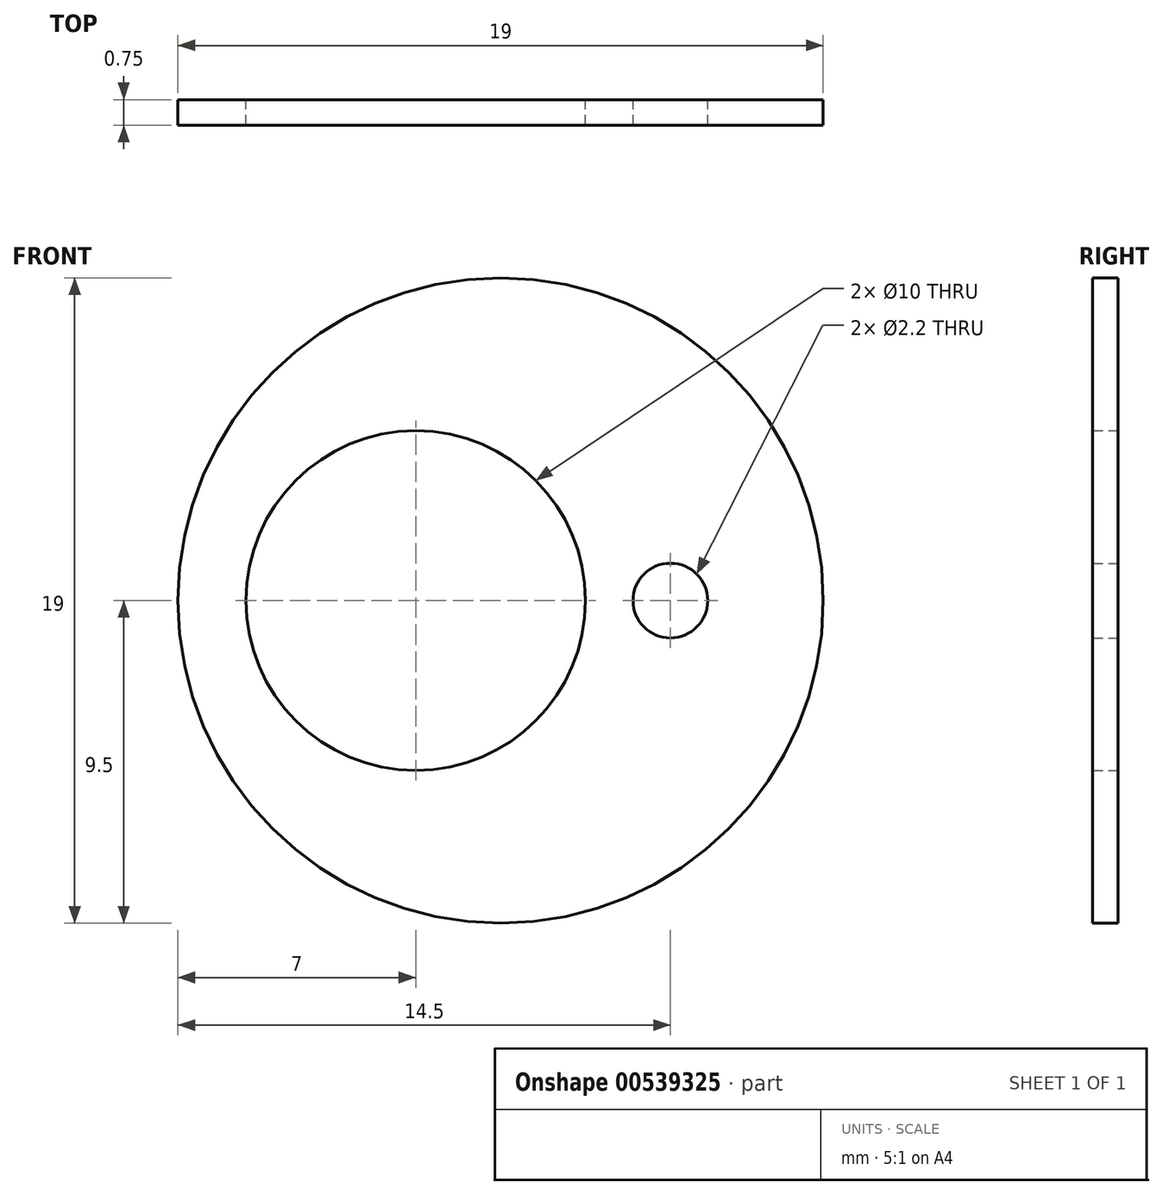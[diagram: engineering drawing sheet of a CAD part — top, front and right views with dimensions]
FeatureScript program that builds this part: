
annotation { "Feature Type Name" : "Feature", "Feature Type Description" : "" }
export const myFeature = defineFeature(function(context is Context, id is Id, definition is map)
    precondition{}
    {
        {
            var Q0;
            Q0=qCreatedBy(makeId("Front.planeOp"),FACE);
            var sketch = newSketch(context, id + "F0", { "sketchPlane" : qUnion([Q0])});
            skCircle(sketch, "E0", {"center": v(0, 0) * mm, "radius": 9.5 * mm});
            skLineSegment(sketch, "E1", {"start": v(0, 9.5) * mm, "end": v(0, -9.5) * mm, "construction": true});
            skLineSegment(sketch, "E2", {"start": v(-9.5, 0) * mm, "end": v(9.5, 0) * mm, "construction": true});
            skPoint(sketch, "E3", {"position": v(5, 0) * mm});
            skPoint(sketch, "E4", {"position": v(-2.5, 0) * mm});
            skCircle(sketch, "E5", {"center": v(-2.5, 0) * mm, "radius": 5 * mm});
            skCircle(sketch, "E6", {"center": v(5, 0) * mm, "radius": 1.1 * mm});
            skSolve(sketch);
        }
        {
            var Q0;
            Q0 = qSketchRegion(id + "F0", true);
            extrude(context, id + "F1", {"entities" : qUnion([Q0]), "depth" : 0.75 * mm, "offsetDistance" : 25 * mm});
        }
    });
